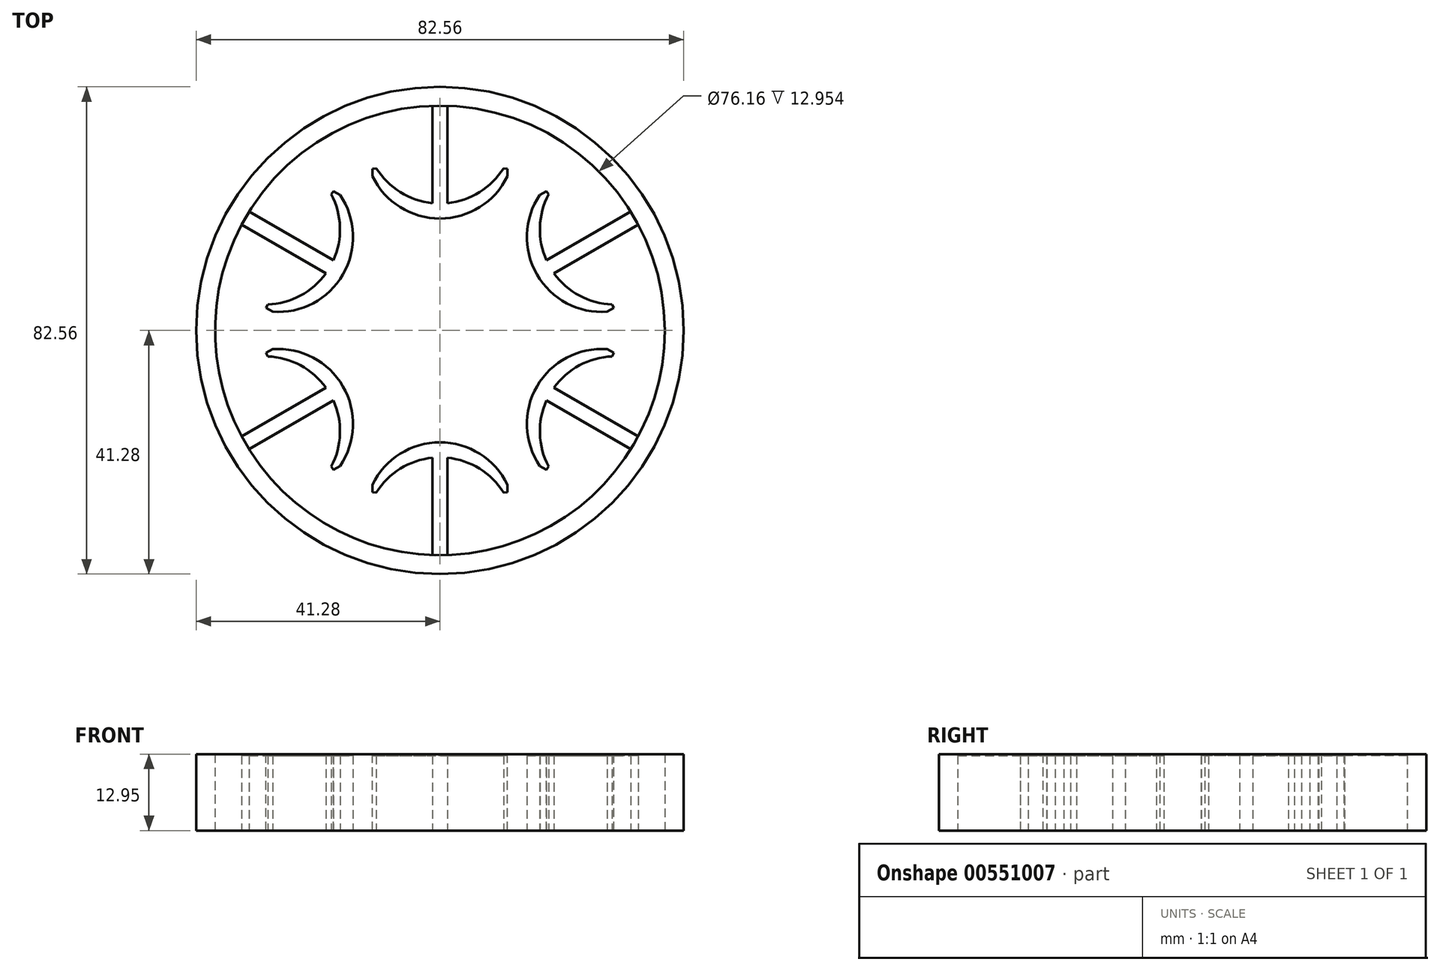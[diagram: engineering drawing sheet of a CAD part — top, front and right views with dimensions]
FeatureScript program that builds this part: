
annotation { "Feature Type Name" : "Feature", "Feature Type Description" : "" }
export const myFeature = defineFeature(function(context is Context, id is Id, definition is map)
    precondition{}
    {
        {
            var Q0;
            Q0=qCreatedBy(makeId("Top.planeOp"),FACE);
            var sketch = newSketch(context, id + "F0", { "sketchPlane" : qUnion([Q0])});
            skCircle(sketch, "E0", {"center": v(0, 0) * mm, "radius": 19.05 * mm});
            skCircle(sketch, "E1", {"center": v(0, 0) * mm, "radius": 38.1 * mm});
            skSolve(sketch);
        }
        {
            var Q0;
            Q0 = qSketchRegion(id + "F0", true);
            extrude(context, id + "F1", {"entities" : qUnion([Q0]), "depth" : 12.7 * mm, "offsetDistance" : 25.4 * mm});
        }
        {
            var Q0;
            Q0=makeQuery(id+"F1.opExtrude","CAP_FACE",FACE,{"disambiguationData":[OSD([sQuery(id+"F0.wireOp",EDGE,"E0"),sQuery(id+"F0.wireOp",EDGE,"E1")])],"isStart":false});
            var sketch = newSketch(context, id + "F2", { "sketchPlane" : qUnion([Q0])});
            skArc(sketch, "E2", {"start": v(-11.43, 26.13) * mm, "mid": v(0, 18.97) * mm, "end": v(11.43, 26.13) * mm});
            skLineSegment(sketch, "E3", {"start": v(-11.43, 28.67) * mm, "end": v(-11.43, 26.13) * mm});
            skLineSegment(sketch, "E4", {"start": v(11.43, 28.67) * mm, "end": v(11.43, 26.13) * mm});
            skLineSegment(sketch, "E5", {"start": v(-1.27, 21.57) * mm, "end": v(-1.27, 38.08) * mm});
            skArc(sketch, "E6", {"start": v(-11.43, 28.67) * mm, "mid": v(0, 21.5) * mm, "end": v(11.43, 28.67) * mm});
            skLineSegment(sketch, "E7", {"start": v(1.27, 38.08) * mm, "end": v(1.27, 21.57) * mm});
            skLineSegment(sketch, "E8", {"start": v(-1.27, 38.08) * mm, "end": v(1.27, 38.08) * mm});
            skLineSegment(sketch, "E9.1.0", {"start": v(-32.34, 20.14) * mm, "end": v(-18.04, 11.88) * mm});
            skLineSegment(sketch, "E9.1.1", {"start": v(-19.31, 9.68) * mm, "end": v(-33.61, 17.94) * mm});
            skLineSegment(sketch, "E9.1.2", {"start": v(-33.61, 17.94) * mm, "end": v(-32.34, 20.14) * mm});
            skArc(sketch, "E9.1.3", {"start": v(-30.54, 4.44) * mm, "mid": v(-18.62, 10.75) * mm, "end": v(-19.11, 24.23) * mm});
            skArc(sketch, "E9.1.4", {"start": v(-28.34, 3.17) * mm, "mid": v(-16.42, 9.48) * mm, "end": v(-16.91, 22.96) * mm});
            skLineSegment(sketch, "E9.1.5", {"start": v(-19.11, 24.23) * mm, "end": v(-16.91, 22.96) * mm});
            skLineSegment(sketch, "E9.1.6", {"start": v(-30.54, 4.44) * mm, "end": v(-28.34, 3.17) * mm});
            skLineSegment(sketch, "E9.2.0", {"start": v(-33.61, -17.94) * mm, "end": v(-19.31, -9.68) * mm});
            skLineSegment(sketch, "E9.2.1", {"start": v(-18.04, -11.88) * mm, "end": v(-32.34, -20.14) * mm});
            skLineSegment(sketch, "E9.2.2", {"start": v(-32.34, -20.14) * mm, "end": v(-33.61, -17.94) * mm});
            skArc(sketch, "E9.2.3", {"start": v(-19.11, -24.23) * mm, "mid": v(-18.62, -10.75) * mm, "end": v(-30.54, -4.44) * mm});
            skArc(sketch, "E9.2.4", {"start": v(-16.91, -22.96) * mm, "mid": v(-16.42, -9.48) * mm, "end": v(-28.34, -3.17) * mm});
            skLineSegment(sketch, "E9.2.5", {"start": v(-30.54, -4.44) * mm, "end": v(-28.34, -3.17) * mm});
            skLineSegment(sketch, "E9.2.6", {"start": v(-19.11, -24.23) * mm, "end": v(-16.91, -22.96) * mm});
            skLineSegment(sketch, "E9.3.0", {"start": v(-1.27, -38.08) * mm, "end": v(-1.27, -21.57) * mm});
            skLineSegment(sketch, "E9.3.1", {"start": v(1.27, -21.57) * mm, "end": v(1.27, -38.08) * mm});
            skLineSegment(sketch, "E9.3.2", {"start": v(1.27, -38.08) * mm, "end": v(-1.27, -38.08) * mm});
            skArc(sketch, "E9.3.3", {"start": v(11.43, -28.67) * mm, "mid": v(0, -21.5) * mm, "end": v(-11.43, -28.67) * mm});
            skArc(sketch, "E9.3.4", {"start": v(11.43, -26.13) * mm, "mid": v(0, -18.97) * mm, "end": v(-11.43, -26.13) * mm});
            skLineSegment(sketch, "E9.3.5", {"start": v(-11.43, -28.67) * mm, "end": v(-11.43, -26.13) * mm});
            skLineSegment(sketch, "E9.3.6", {"start": v(11.43, -28.67) * mm, "end": v(11.43, -26.13) * mm});
            skLineSegment(sketch, "E9.4.0", {"start": v(32.34, -20.14) * mm, "end": v(18.04, -11.88) * mm});
            skLineSegment(sketch, "E9.4.1", {"start": v(19.31, -9.68) * mm, "end": v(33.61, -17.94) * mm});
            skLineSegment(sketch, "E9.4.2", {"start": v(33.61, -17.94) * mm, "end": v(32.34, -20.14) * mm});
            skArc(sketch, "E9.4.3", {"start": v(30.54, -4.44) * mm, "mid": v(18.62, -10.75) * mm, "end": v(19.11, -24.23) * mm});
            skArc(sketch, "E9.4.4", {"start": v(28.34, -3.17) * mm, "mid": v(16.42, -9.48) * mm, "end": v(16.91, -22.96) * mm});
            skLineSegment(sketch, "E9.4.5", {"start": v(19.11, -24.23) * mm, "end": v(16.91, -22.96) * mm});
            skLineSegment(sketch, "E9.4.6", {"start": v(30.54, -4.44) * mm, "end": v(28.34, -3.17) * mm});
            skLineSegment(sketch, "E9.5.0", {"start": v(33.61, 17.94) * mm, "end": v(19.31, 9.68) * mm});
            skLineSegment(sketch, "E9.5.1", {"start": v(18.04, 11.88) * mm, "end": v(32.34, 20.14) * mm});
            skLineSegment(sketch, "E9.5.2", {"start": v(32.34, 20.14) * mm, "end": v(33.61, 17.94) * mm});
            skArc(sketch, "E9.5.3", {"start": v(19.11, 24.23) * mm, "mid": v(18.62, 10.75) * mm, "end": v(30.54, 4.44) * mm});
            skArc(sketch, "E9.5.4", {"start": v(16.91, 22.96) * mm, "mid": v(16.42, 9.48) * mm, "end": v(28.34, 3.17) * mm});
            skLineSegment(sketch, "E9.5.5", {"start": v(30.54, 4.44) * mm, "end": v(28.34, 3.17) * mm});
            skLineSegment(sketch, "E9.5.6", {"start": v(19.11, 24.23) * mm, "end": v(16.91, 22.96) * mm});
            skPoint(sketch, "E9.center", {"position": v(0, 0) * mm});
            skSolve(sketch);
        }
        {
            var Q0;
            Q0 = qSketchRegion(id + "F2", true);
            extrude(context, id + "F3", {"entities" : qUnion([Q0]), "operationType" : NewBodyOperationType.ADD, "depth" : 12.7 * mm, "offsetDistance" : 25.4 * mm});
        }
        {
            var Q0;
            Q0=makeQuery(id+"F1.opExtrude","CAP_FACE",FACE,{"disambiguationData":[OSD([sQuery(id+"F0.wireOp",EDGE,"E0"),sQuery(id+"F0.wireOp",EDGE,"E1")])],"isStart":true});
            extrude(context, id + "F4", {"entities" : qUnion([Q0]), "operationType" : NewBodyOperationType.REMOVE, "oppositeDirection" : true, "depth" : 12.7 * mm, "offsetDistance" : 25.4 * mm});
        }
        {
            var Q0;
            Q0=makeQuery(id+"F4.boolean.opBoolean","MERGE",FACE,{"derivedFrom":[makeQuery(id+"F3.opExtrude","CAP_FACE",FACE,{"disambiguationData":[OSD([sQuery(id+"F2.wireOp",EDGE,"E9.2.0"),sQuery(id+"F2.wireOp",EDGE,"E9.2.1"),sQuery(id+"F2.wireOp",EDGE,"E9.2.2"),sQuery(id+"F2.wireOp",EDGE,"E9.2.3"),sQuery(id+"F2.wireOp",EDGE,"E9.2.4"),sQuery(id+"F2.wireOp",EDGE,"E9.2.5"),sQuery(id+"F2.wireOp",EDGE,"E9.2.6")])],"isStart":true}),makeQuery(id+"F4.opExtrude","CAP_FACE",FACE,{"disambiguationData":[OSD([sQuery(id+"F0.wireOp",EDGE,"E0"),sQuery(id+"F0.wireOp",EDGE,"E1")])],"isStart":false})]});
            var sketch = newSketch(context, id + "F5", { "sketchPlane" : qUnion([Q0])});
            skCircle(sketch, "E10", {"center": v(0, 0) * mm, "radius": 41.28 * mm});
            skCircle(sketch, "E11", {"center": v(0, 0) * mm, "radius": 38.08 * mm});
            skSolve(sketch);
        }
        {
            var Q0;
            Q0 = qSketchRegion(id + "F5", true);
            extrude(context, id + "F6", {"entities" : qUnion([Q0]), "operationType" : NewBodyOperationType.ADD, "oppositeDirection" : true, "depth" : 12.7 * mm, "offsetDistance" : 25.4 * mm});
        }
        {
            var Q0;
            Q0=makeQuery(id+"F6.boolean.opBoolean","MERGE",FACE,{"derivedFrom":[makeQuery(id+"F3.opExtrude","CAP_FACE",FACE,{"disambiguationData":[OSD([sQuery(id+"F2.wireOp",EDGE,"E2"),sQuery(id+"F2.wireOp",EDGE,"E3"),sQuery(id+"F2.wireOp",EDGE,"E4"),sQuery(id+"F2.wireOp",EDGE,"E5"),sQuery(id+"F2.wireOp",EDGE,"E6"),sQuery(id+"F2.wireOp",EDGE,"E7"),sQuery(id+"F2.wireOp",EDGE,"E8")])],"isStart":false}),makeQuery(id+"F3.opExtrude","CAP_FACE",FACE,{"disambiguationData":[OSD([sQuery(id+"F2.wireOp",EDGE,"E9.1.0"),sQuery(id+"F2.wireOp",EDGE,"E9.1.1"),sQuery(id+"F2.wireOp",EDGE,"E9.1.2"),sQuery(id+"F2.wireOp",EDGE,"E9.1.3"),sQuery(id+"F2.wireOp",EDGE,"E9.1.4"),sQuery(id+"F2.wireOp",EDGE,"E9.1.5"),sQuery(id+"F2.wireOp",EDGE,"E9.1.6")])],"isStart":false}),makeQuery(id+"F3.opExtrude","CAP_FACE",FACE,{"disambiguationData":[OSD([sQuery(id+"F2.wireOp",EDGE,"E9.2.0"),sQuery(id+"F2.wireOp",EDGE,"E9.2.1"),sQuery(id+"F2.wireOp",EDGE,"E9.2.2"),sQuery(id+"F2.wireOp",EDGE,"E9.2.3"),sQuery(id+"F2.wireOp",EDGE,"E9.2.4"),sQuery(id+"F2.wireOp",EDGE,"E9.2.5"),sQuery(id+"F2.wireOp",EDGE,"E9.2.6")])],"isStart":false}),makeQuery(id+"F3.opExtrude","CAP_FACE",FACE,{"disambiguationData":[OSD([sQuery(id+"F2.wireOp",EDGE,"E9.3.0"),sQuery(id+"F2.wireOp",EDGE,"E9.3.1"),sQuery(id+"F2.wireOp",EDGE,"E9.3.2"),sQuery(id+"F2.wireOp",EDGE,"E9.3.3"),sQuery(id+"F2.wireOp",EDGE,"E9.3.4"),sQuery(id+"F2.wireOp",EDGE,"E9.3.5"),sQuery(id+"F2.wireOp",EDGE,"E9.3.6")])],"isStart":false}),makeQuery(id+"F3.opExtrude","CAP_FACE",FACE,{"disambiguationData":[OSD([sQuery(id+"F2.wireOp",EDGE,"E9.4.0"),sQuery(id+"F2.wireOp",EDGE,"E9.4.1"),sQuery(id+"F2.wireOp",EDGE,"E9.4.2"),sQuery(id+"F2.wireOp",EDGE,"E9.4.3"),sQuery(id+"F2.wireOp",EDGE,"E9.4.4"),sQuery(id+"F2.wireOp",EDGE,"E9.4.5"),sQuery(id+"F2.wireOp",EDGE,"E9.4.6")])],"isStart":false}),makeQuery(id+"F3.opExtrude","CAP_FACE",FACE,{"disambiguationData":[OSD([sQuery(id+"F2.wireOp",EDGE,"E9.5.0"),sQuery(id+"F2.wireOp",EDGE,"E9.5.1"),sQuery(id+"F2.wireOp",EDGE,"E9.5.2"),sQuery(id+"F2.wireOp",EDGE,"E9.5.3"),sQuery(id+"F2.wireOp",EDGE,"E9.5.4"),sQuery(id+"F2.wireOp",EDGE,"E9.5.5"),sQuery(id+"F2.wireOp",EDGE,"E9.5.6")])],"isStart":false}),makeQuery(id+"F6.opExtrude","CAP_FACE",FACE,{"disambiguationData":[OSD([sQuery(id+"F5.wireOp",EDGE,"E10"),sQuery(id+"F5.wireOp",EDGE,"E11")])],"isStart":false})]});
            var sketch = newSketch(context, id + "F7", { "sketchPlane" : qUnion([Q0])});
            skCircle(sketch, "E12", {"center": v(0, 0) * mm, "radius": 38.08 * mm});
            skCircle(sketch, "E13", {"center": v(0, 0) * mm, "radius": 41.28 * mm});
            skCircle(sketch, "E14", {"center": v(0, 0) * mm, "radius": 21.6 * mm});
            skSolve(sketch);
        }
        {
            var Q0;
            Q0 = qSketchRegion(id + "F7", true);
            extrude(context, id + "F8", {"entities" : qUnion([Q0]), "operationType" : NewBodyOperationType.ADD, "depth" : 0.25 * mm, "offsetDistance" : 25.4 * mm});
        }
        {
            var Q0;
            {var subQ0=sQuery(id+"F2.wireOp",EDGE,"E4");var subQ1=sQuery(id+"F2.wireOp",EDGE,"E3");var subQ2=sQuery(id+"F2.wireOp",EDGE,"E5");var subQ3=sQuery(id+"F5.wireOp",EDGE,"E11");var subQ4=sQuery(id+"F2.wireOp",EDGE,"E2");var subQ5=sQuery(id+"F2.wireOp",EDGE,"E6");var subQ6=sQuery(id+"F2.wireOp",EDGE,"E7");Q0=makeQuery(id+"F8.boolean.opBoolean","SPLIT",FACE,{"disambiguationData":[TD([makeQuery(id+"F3.opExtrude","SWEPT_FACE",FACE,{"disambiguationData":[OSD([subQ4])]})])],"derivedFrom":makeQuery(id+"F6.boolean.opBoolean","MERGE",FACE,{"derivedFrom":[makeQuery(id+"F3.opExtrude","CAP_FACE",FACE,{"disambiguationData":[OSD([subQ4,subQ1,subQ0,subQ2,subQ5,subQ6,sQuery(id+"F2.wireOp",EDGE,"E8")])],"isStart":false}),makeQuery(id+"F3.opExtrude","CAP_FACE",FACE,{"disambiguationData":[OSD([sQuery(id+"F2.wireOp",EDGE,"E9.1.0"),sQuery(id+"F2.wireOp",EDGE,"E9.1.1"),sQuery(id+"F2.wireOp",EDGE,"E9.1.2"),sQuery(id+"F2.wireOp",EDGE,"E9.1.3"),sQuery(id+"F2.wireOp",EDGE,"E9.1.4"),sQuery(id+"F2.wireOp",EDGE,"E9.1.5"),sQuery(id+"F2.wireOp",EDGE,"E9.1.6")])],"isStart":false}),makeQuery(id+"F3.opExtrude","CAP_FACE",FACE,{"disambiguationData":[OSD([sQuery(id+"F2.wireOp",EDGE,"E9.2.0"),sQuery(id+"F2.wireOp",EDGE,"E9.2.1"),sQuery(id+"F2.wireOp",EDGE,"E9.2.2"),sQuery(id+"F2.wireOp",EDGE,"E9.2.3"),sQuery(id+"F2.wireOp",EDGE,"E9.2.4"),sQuery(id+"F2.wireOp",EDGE,"E9.2.5"),sQuery(id+"F2.wireOp",EDGE,"E9.2.6")])],"isStart":false}),makeQuery(id+"F3.opExtrude","CAP_FACE",FACE,{"disambiguationData":[OSD([sQuery(id+"F2.wireOp",EDGE,"E9.3.0"),sQuery(id+"F2.wireOp",EDGE,"E9.3.1"),sQuery(id+"F2.wireOp",EDGE,"E9.3.2"),sQuery(id+"F2.wireOp",EDGE,"E9.3.3"),sQuery(id+"F2.wireOp",EDGE,"E9.3.4"),sQuery(id+"F2.wireOp",EDGE,"E9.3.5"),sQuery(id+"F2.wireOp",EDGE,"E9.3.6")])],"isStart":false}),makeQuery(id+"F3.opExtrude","CAP_FACE",FACE,{"disambiguationData":[OSD([sQuery(id+"F2.wireOp",EDGE,"E9.4.0"),sQuery(id+"F2.wireOp",EDGE,"E9.4.1"),sQuery(id+"F2.wireOp",EDGE,"E9.4.2"),sQuery(id+"F2.wireOp",EDGE,"E9.4.3"),sQuery(id+"F2.wireOp",EDGE,"E9.4.4"),sQuery(id+"F2.wireOp",EDGE,"E9.4.5"),sQuery(id+"F2.wireOp",EDGE,"E9.4.6")])],"isStart":false}),makeQuery(id+"F3.opExtrude","CAP_FACE",FACE,{"disambiguationData":[OSD([sQuery(id+"F2.wireOp",EDGE,"E9.5.0"),sQuery(id+"F2.wireOp",EDGE,"E9.5.1"),sQuery(id+"F2.wireOp",EDGE,"E9.5.2"),sQuery(id+"F2.wireOp",EDGE,"E9.5.3"),sQuery(id+"F2.wireOp",EDGE,"E9.5.4"),sQuery(id+"F2.wireOp",EDGE,"E9.5.5"),sQuery(id+"F2.wireOp",EDGE,"E9.5.6")])],"isStart":false}),makeQuery(id+"F6.opExtrude","CAP_FACE",FACE,{"disambiguationData":[OSD([sQuery(id+"F5.wireOp",EDGE,"E10"),subQ3])],"isStart":false})]})});}
            var sketch = newSketch(context, id + "F9", { "sketchPlane" : qUnion([Q0])});
            skArc(sketch, "E15", {"start": v(-11.43, 27.4) * mm, "mid": v(-15.12, 26.2) * mm, "end": v(-18.01, 23.6) * mm});
            skPoint(sketch, "E15.startSnap0", {"position": v(-11.43, 27.4) * mm});
            skLineSegment(sketch, "E16", {"start": v(-18.01, 23.6) * mm, "end": v(-21.23, 19.2) * mm});
            skLineSegment(sketch, "E17", {"start": v(-11.43, 27.4) * mm, "end": v(-9.02, 27.66) * mm});
            skLineSegment(sketch, "E18", {"start": v(-9.02, 27.66) * mm, "end": v(-9.26, 33) * mm});
            skLineSegment(sketch, "E19", {"start": v(-9.26, 33) * mm, "end": v(-21.96, 26.43) * mm});
            skLineSegment(sketch, "E20", {"start": v(-21.96, 26.43) * mm, "end": v(-21.23, 19.2) * mm});
            skArc(sketch, "E21.1.0", {"start": v(-29.44, 3.8) * mm, "mid": v(-30.24, 0) * mm, "end": v(-29.44, -3.8) * mm});
            skLineSegment(sketch, "E21.1.1", {"start": v(-29.44, 3.8) * mm, "end": v(-28.47, 6.02) * mm});
            skLineSegment(sketch, "E21.1.2", {"start": v(-28.47, 6.02) * mm, "end": v(-33.2, 8.47) * mm});
            skLineSegment(sketch, "E21.1.3", {"start": v(-33.2, 8.47) * mm, "end": v(-33.87, -5.8) * mm});
            skLineSegment(sketch, "E21.1.4", {"start": v(-33.87, -5.8) * mm, "end": v(-27.25, -8.79) * mm});
            skLineSegment(sketch, "E21.1.5", {"start": v(-29.44, -3.8) * mm, "end": v(-27.25, -8.79) * mm});
            skArc(sketch, "E21.2.0", {"start": v(-18.01, -23.6) * mm, "mid": v(-15.12, -26.2) * mm, "end": v(-11.43, -27.4) * mm});
            skLineSegment(sketch, "E21.2.1", {"start": v(-18.01, -23.6) * mm, "end": v(-19.45, -21.64) * mm});
            skLineSegment(sketch, "E21.2.2", {"start": v(-19.45, -21.64) * mm, "end": v(-23.94, -24.52) * mm});
            skLineSegment(sketch, "E21.2.3", {"start": v(-23.94, -24.52) * mm, "end": v(-11.91, -32.23) * mm});
            skLineSegment(sketch, "E21.2.4", {"start": v(-11.91, -32.23) * mm, "end": v(-6.02, -28) * mm});
            skLineSegment(sketch, "E21.2.5", {"start": v(-11.43, -27.4) * mm, "end": v(-6.02, -28) * mm});
            skArc(sketch, "E21.3.0", {"start": v(11.43, -27.4) * mm, "mid": v(15.12, -26.2) * mm, "end": v(18.01, -23.6) * mm});
            skLineSegment(sketch, "E21.3.1", {"start": v(11.43, -27.4) * mm, "end": v(9.02, -27.66) * mm});
            skLineSegment(sketch, "E21.3.2", {"start": v(9.02, -27.66) * mm, "end": v(9.26, -33) * mm});
            skLineSegment(sketch, "E21.3.3", {"start": v(9.26, -33) * mm, "end": v(21.96, -26.43) * mm});
            skLineSegment(sketch, "E21.3.4", {"start": v(21.96, -26.43) * mm, "end": v(21.23, -19.2) * mm});
            skLineSegment(sketch, "E21.3.5", {"start": v(18.01, -23.6) * mm, "end": v(21.23, -19.2) * mm});
            skArc(sketch, "E21.4.0", {"start": v(29.44, -3.8) * mm, "mid": v(30.24, 0) * mm, "end": v(29.44, 3.8) * mm});
            skLineSegment(sketch, "E21.4.1", {"start": v(29.44, -3.8) * mm, "end": v(28.47, -6.02) * mm});
            skLineSegment(sketch, "E21.4.2", {"start": v(28.47, -6.02) * mm, "end": v(33.2, -8.47) * mm});
            skLineSegment(sketch, "E21.4.3", {"start": v(33.2, -8.47) * mm, "end": v(33.87, 5.8) * mm});
            skLineSegment(sketch, "E21.4.4", {"start": v(33.87, 5.8) * mm, "end": v(27.25, 8.79) * mm});
            skLineSegment(sketch, "E21.4.5", {"start": v(29.44, 3.8) * mm, "end": v(27.25, 8.79) * mm});
            skArc(sketch, "E21.5.0", {"start": v(18.01, 23.6) * mm, "mid": v(15.12, 26.2) * mm, "end": v(11.43, 27.4) * mm});
            skLineSegment(sketch, "E21.5.1", {"start": v(18.01, 23.6) * mm, "end": v(19.45, 21.64) * mm});
            skLineSegment(sketch, "E21.5.2", {"start": v(19.45, 21.64) * mm, "end": v(23.94, 24.52) * mm});
            skLineSegment(sketch, "E21.5.3", {"start": v(23.94, 24.52) * mm, "end": v(11.91, 32.23) * mm});
            skLineSegment(sketch, "E21.5.4", {"start": v(11.91, 32.23) * mm, "end": v(6.02, 28) * mm});
            skLineSegment(sketch, "E21.5.5", {"start": v(11.43, 27.4) * mm, "end": v(6.02, 28) * mm});
            skPoint(sketch, "E21.center", {"position": v(0, 0) * mm});
            skSolve(sketch);
        }
        {
            var Q0;
            Q0 = qSketchRegion(id + "F9", true);
            extrude(context, id + "F10", {"entities" : qUnion([Q0]), "operationType" : NewBodyOperationType.REMOVE, "endBound" : BoundingType.THROUGH_ALL, "oppositeDirection" : true, "depth" : 25.4 * mm, "offsetDistance" : 25.4 * mm});
        }
    });
